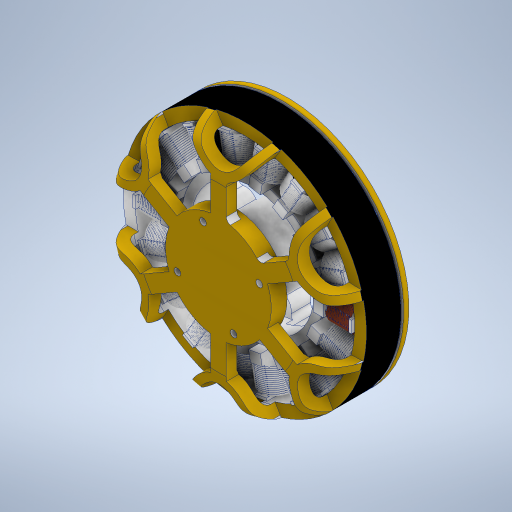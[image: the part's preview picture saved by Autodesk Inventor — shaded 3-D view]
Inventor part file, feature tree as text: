
AUTODESK INVENTOR PART (.ipt)
format: ipt  version: 2023 (Build 270158000, 158)  size: 15,429,632 bytes
history: native  units: in
note: dims shown in document units (in); Inventor stores cm internally (conversion verified against a paired STEP export)
features: sketch x8, extrude x7, pattern_circular x5, projected_geometry x4, fillet x2, revolve x1, helix x1
ambient origin geometry x8: Origin, YZ Plane, XZ Plane, XY Plane, X Axis, Y Axis, Z Axis, Center Point
bodies: Solid1 (feature_tree)
feature tree (28):
  revolve  "Revolution1"  [1 undecoded]
  sketch  "Sketch2"  dims[d2=0.748in d3=0.1575in d4=0.4134in]
  extrude  "Extrusion1"  Depth=0.1575in
  fillet  "Fillet1"  Radius=0.4134in
  pattern_circular  "Circular Pattern1"  [2 undecoded]
  extrude  "Extrusion2"  Depth=0.0236in
  pattern_circular  "Circular Pattern2"  Count=2  [1 undecoded]
  extrude  "Extrusion3"  Depth=0.0236in
  sketch  "Sketch4"  dims[d7=0.1772in]
  extrude  "Extrusion4"  Depth=0.0236in
  fillet  "Fillet2"  Radius=1.063in
  extrude  "Extrusion5"  Depth=0.0236in
  pattern_circular  "Circular Pattern4"  [2 undecoded]
  extrude  "Extrusion6"  TaperAngle=90.0deg  [1 undecoded]
  pattern_circular  "Circular Pattern5"  [2 undecoded]
  extrude  "Extrusion7"  Depth=0.0236in
  helix  "Coil1"  [1 undecoded]
  pattern_circular  "Circular Pattern6"  [2 undecoded]
  sketch  "Sketch1"  dims[d0=0.1772in d1=0.5315in]
  projected_geometry  "Projected Loop1"
  sketch  "Sketch3"  dims[d6=0.1575in]
  sketch  "Sketch5"  dims[d8=0.0394in]
  projected_geometry  "Projected Loop2"
  sketch  "Sketch6"  dims[d9=0.0394in]
  sketch  "Sketch7"  dims[d10=0.1575in]
  projected_geometry  "Projected Loop3"
  projected_geometry  "Projected Loop4"
  sketch  "Sketch8"  dims[d11=0.1969in d12=0.4331in d13=0.4331in d14=0.7874in d15=0.2362in d17=0.0787in d19=1.063in d20=0.8661in d22=0.17in d23=90.0deg d24=0.6102in d25=0.1378in d26=0.2953in d27=0.0394in d28=0.6102in d29=0.5079in d30=0.8465in d31=1.378in d32=0.4232in d33=0.1181in d34=2.3622in d36=360.0deg d40=0.2362in d41=0.1181in d42=1.5748in d43=2.3622in d45=360.0deg d47=2.3622in d49=360.0deg d51=0.3937in d52=0.0in d53=0.0787in d54=2.3622in d55=360.0deg d57=0.3937in d58=0.0in d59=2.3622in d60=360.0deg d62=1.2992in d63=0.0984in d64=1.5748in d66=360.0deg d68=0.3937in d69=0.0in d70=1.8898in d71=1.0157in d72=0.1299in d73=1.5748in d75=360.0deg d77=1.5787in d78=0.1181in d79=0.1969in d80=0.0984in d81=1.5748in d83=360.0deg d85=0.3937in d86=0.0in d87=0.0689in d91=0.3937in d92=0.0in d93=1.5748in d94=360.0deg d97=2.126in d99=0.0787in d102=0.5906in d108=0.2362in d110=0.4528in d111=0.1181in d113=0.3051in d115=0.2362in d116=0.315in d118=0.748in d120=1.622in d121=45.0deg d122=0.2362in d123=0.2362in d124=0.1181in d125=1.2008in d126=0.1181in d127=0.2362in d128=0.0in d129=1.5748in d130=360.0deg d132=0.374in d133=0.1575in d134=0.0394in d135=0.0394in d136=0.1575in d137=0.3937in d138=0.0394in d139=0.1181in d140=0.1772in d141=0.0in d143=0.0197in d144=0.0236in d145=0.3543in d146=53.1496in d147=0.0in d148=90.0deg d149=90.0deg d150=0.0in d151=0.0in d152=7.0866in d153=360.0deg]
note: 12 required parameter values undecoded (feature->parameter linkage not recoverable at this tier; creation-order binding heuristic only, values carry confidence <= 0.55)